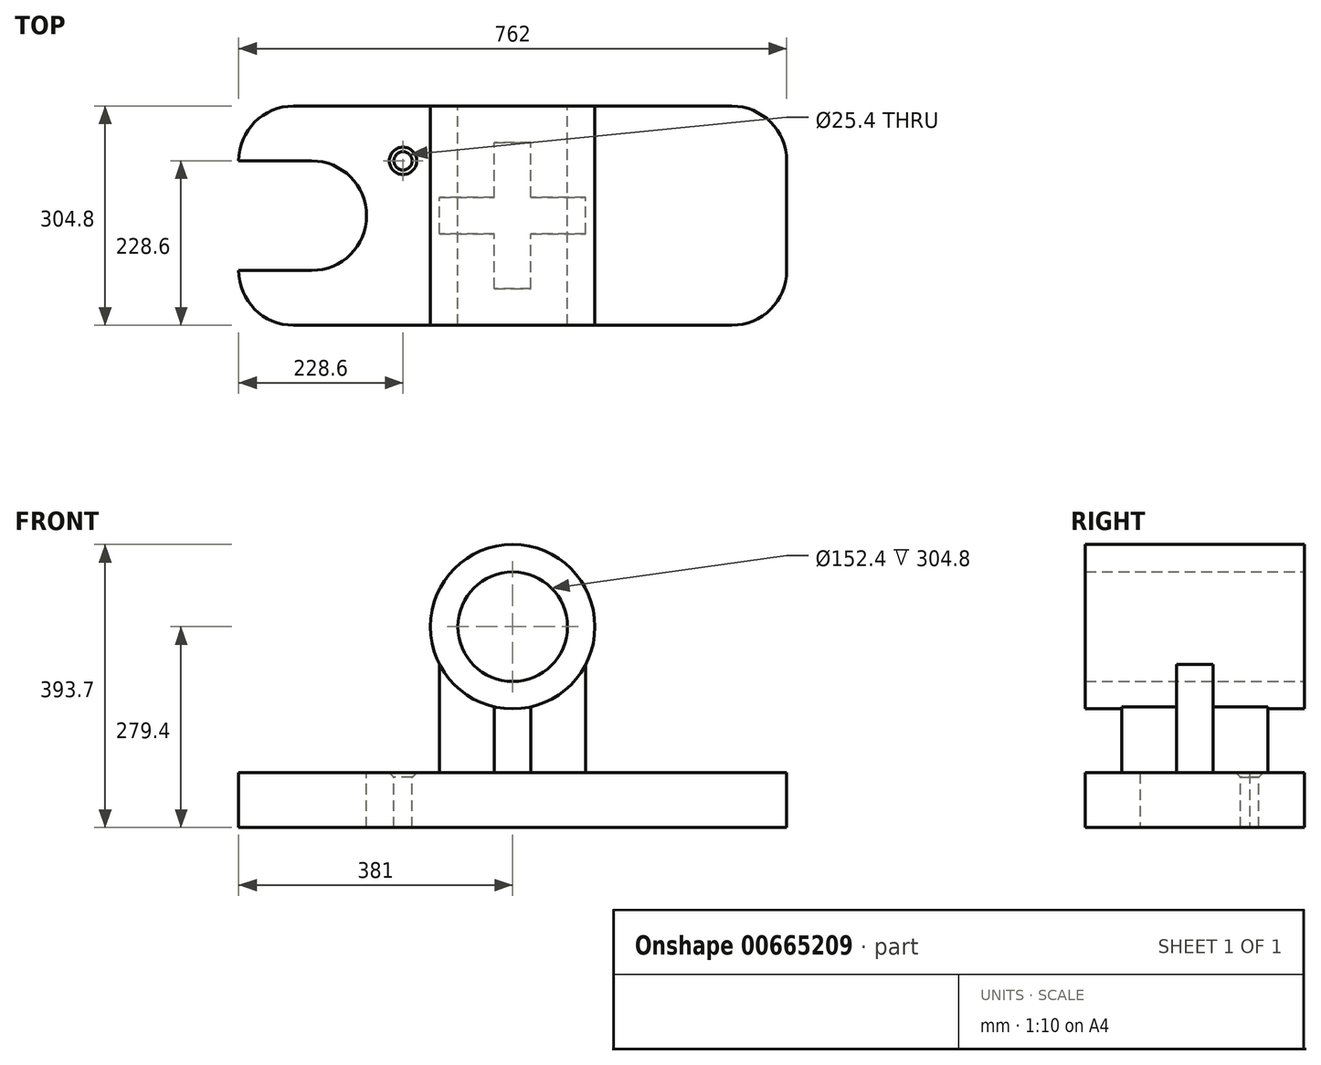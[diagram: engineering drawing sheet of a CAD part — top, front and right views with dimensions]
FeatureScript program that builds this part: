
annotation { "Feature Type Name" : "Feature", "Feature Type Description" : "" }
export const myFeature = defineFeature(function(context is Context, id is Id, definition is map)
    precondition{}
    {
        {
            var Q0;
            Q0=qCreatedBy(makeId("Top.planeOp"),FACE);
            var sketch = newSketch(context, id + "F0", { "sketchPlane" : qUnion([Q0])});
            skLineSegment(sketch, "E0.bottom", {"start": v(381, -152.4) * mm, "end": v(-381, -152.4) * mm});
            skLineSegment(sketch, "E0.top", {"start": v(381, 152.4) * mm, "end": v(-381, 152.4) * mm});
            skLineSegment(sketch, "E0.left", {"start": v(381, -152.4) * mm, "end": v(381, 152.4) * mm});
            skLineSegment(sketch, "E0.right", {"start": v(-381, -152.4) * mm, "end": v(-381, 152.4) * mm});
            skPoint(sketch, "E0.middle", {"position": v(0, 0) * mm});
            skSolve(sketch);
        }
        {
            var Q0;
            Q0=makeQuery(id+"F0.imprint","IMPRINT",FACE,{"disambiguationData":[TD([[makeQuery(id+"F0.imprint","IMPRINT",EDGE,{"derivedFrom":sQuery(id+"F0.wireOp",EDGE,"E0.bottom")}),-1.0]])]});
            extrude(context, id + "F1", {"entities" : qUnion([Q0]), "depth" : 76.2 * mm, "offsetDistance" : 25.4 * mm});
        }
        {
            var Q0;
            Q0=makeQuery(id+"F1.opExtrude","CAP_FACE",FACE,{"disambiguationData":[OSD([sQuery(id+"F0.wireOp",EDGE,"E0.bottom"),sQuery(id+"F0.wireOp",EDGE,"E0.top"),sQuery(id+"F0.wireOp",EDGE,"E0.left"),sQuery(id+"F0.wireOp",EDGE,"E0.right")])],"isStart":false});
            var sketch = newSketch(context, id + "F2", { "sketchPlane" : qUnion([Q0])});
            skLineSegment(sketch, "E1.0", {"start": v(101.6, 25.4) * mm, "end": v(25.4, 25.4) * mm});
            skLineSegment(sketch, "E2.0", {"start": v(101.6, -25.4) * mm, "end": v(25.4, -25.4) * mm});
            skLineSegment(sketch, "E3.0", {"start": v(101.6, -25.4) * mm, "end": v(101.6, 25.4) * mm});
            skLineSegment(sketch, "E4.0", {"start": v(-101.6, -25.4) * mm, "end": v(-101.6, 25.4) * mm});
            skLineSegment(sketch, "E5.0", {"start": v(-25.4, -101.6) * mm, "end": v(-25.4, -25.4) * mm});
            skLineSegment(sketch, "E6.0", {"start": v(25.4, -101.6) * mm, "end": v(25.4, -25.4) * mm});
            skLineSegment(sketch, "E7.trimOffspring", {"start": v(25.4, 101.6) * mm, "end": v(-25.4, 101.6) * mm});
            skLineSegment(sketch, "E8.trimOffspring", {"start": v(25.4, -101.6) * mm, "end": v(-25.4, -101.6) * mm});
            skLineSegment(sketch, "E9.trimOffspring", {"start": v(-25.4, 25.4) * mm, "end": v(-101.6, 25.4) * mm});
            skLineSegment(sketch, "E10.trimOffspring", {"start": v(-25.4, -25.4) * mm, "end": v(-101.6, -25.4) * mm});
            skLineSegment(sketch, "E11.trimOffspring", {"start": v(-25.4, 25.4) * mm, "end": v(-25.4, 101.6) * mm});
            skLineSegment(sketch, "E12.trimOffspring", {"start": v(25.4, 25.4) * mm, "end": v(25.4, 101.6) * mm});
            skSolve(sketch);
        }
        {
            var Q0;
            Q0=makeQuery(id+"F2.imprint","IMPRINT",FACE,{"disambiguationData":[TD([[makeQuery(id+"F2.imprint","IMPRINT",EDGE,{"derivedFrom":sQuery(id+"F2.wireOp",EDGE,"E1.0")}),1.0]])]});
            extrude(context, id + "F3", {"entities" : qUnion([Q0]), "operationType" : NewBodyOperationType.ADD, "depth" : 203.2 * mm, "offsetDistance" : 25.4 * mm});
        }
        {
            var Q0;
            Q0=qCreatedBy(makeId("Front.planeOp"),FACE);
            var sketch = newSketch(context, id + "F4", { "sketchPlane" : qUnion([Q0])});
            skPoint(sketch, "E13.0", {"position": v(0, 279.4) * mm});
            skCircle(sketch, "E14", {"center": v(0, 279.4) * mm, "radius": 114.3 * mm});
            skCircle(sketch, "E15", {"center": v(0, 279.4) * mm, "radius": 76.2 * mm});
            skSolve(sketch);
        }
        {
            var Q0;
            Q0=makeQuery(id+"F4.imprint","IMPRINT",FACE,{"disambiguationData":[TD([[makeQuery(id+"F4.imprint","IMPRINT",EDGE,{"derivedFrom":sQuery(id+"F4.wireOp",EDGE,"E14")}),1.0]])]});
            extrude(context, id + "F5", {"entities" : qUnion([Q0]), "operationType" : NewBodyOperationType.ADD, "endBound" : BoundingType.SYMMETRIC, "depth" : 304.8 * mm, "offsetDistance" : 25.4 * mm});
        }
        {
            var Q0;
            Q0=makeQuery(id+"F4.imprint","IMPRINT",FACE,{"disambiguationData":[TD([[makeQuery(id+"F4.imprint","IMPRINT",EDGE,{"derivedFrom":sQuery(id+"F4.wireOp",EDGE,"E15")}),1.0]])]});
            extrude(context, id + "F6", {"entities" : qUnion([Q0]), "operationType" : NewBodyOperationType.REMOVE, "endBound" : BoundingType.SYMMETRIC, "oppositeDirection" : true, "depth" : 304.8 * mm, "offsetDistance" : 25.4 * mm});
        }
        {
            var Q0;
            Q0=makeQuery(id+"F1.opExtrude","CAP_FACE",FACE,{"disambiguationData":[OSD([sQuery(id+"F0.wireOp",EDGE,"E0.bottom"),sQuery(id+"F0.wireOp",EDGE,"E0.top"),sQuery(id+"F0.wireOp",EDGE,"E0.left"),sQuery(id+"F0.wireOp",EDGE,"E0.right")])],"isStart":false});
            var sketch = newSketch(context, id + "F7", { "sketchPlane" : qUnion([Q0])});
            skSolve(sketch);
        }
        {
            var Q0;
            Q0=makeQuery(id+"F1.opExtrude","SWEPT_EDGE",EDGE,{"disambiguationData":[OSD([sQuery(id+"F0.wireOp",EDGE,"E0.top"),sQuery(id+"F0.wireOp",EDGE,"E0.left")])]});
            var Q1;
            Q1=makeQuery(id+"F1.opExtrude","SWEPT_EDGE",EDGE,{"disambiguationData":[OSD([sQuery(id+"F0.wireOp",EDGE,"E0.top"),sQuery(id+"F0.wireOp",EDGE,"E0.right")])]});
            var Q2;
            Q2=makeQuery(id+"F1.opExtrude","SWEPT_EDGE",EDGE,{"disambiguationData":[OSD([sQuery(id+"F0.wireOp",EDGE,"E0.bottom"),sQuery(id+"F0.wireOp",EDGE,"E0.left")])]});
            var Q3;
            Q3=makeQuery(id+"F1.opExtrude","SWEPT_EDGE",EDGE,{"disambiguationData":[OSD([sQuery(id+"F0.wireOp",EDGE,"E0.bottom"),sQuery(id+"F0.wireOp",EDGE,"E0.right")])]});
            fillet(context, id + "F8", {"entities" : qUnion([Q0, Q1, Q2, Q3]), "radius" : 76.2 * mm, "tangentPropagation" : true, "allowEdgeOverflow" : false});
        }
        {
            var Q0;
            Q0=makeQuery(id+"F7.imprint","IMPRINT",FACE,{"disambiguationData":[TD([[makeQuery(id+"F7.imprint","IMPRINT",EDGE,{"derivedFrom":makeQuery(id+"F1.opExtrude","CAP_EDGE",EDGE,{"disambiguationData":[OSD([sQuery(id+"F0.wireOp",EDGE,"E0.bottom")])],"isStart":false})}),-1.0]])]});
            var sketch = newSketch(context, id + "F9", { "sketchPlane" : qUnion([Q0])});
            skArc(sketch, "E16", {"start": v(-279.4, -76.2) * mm, "mid": v(-203.2, 0) * mm, "end": v(-279.4, 76.2) * mm});
            skLineSegment(sketch, "E17", {"start": v(-279.4, 76.2) * mm, "end": v(-381, 76.2) * mm});
            skLineSegment(sketch, "E18", {"start": v(-279.4, -76.2) * mm, "end": v(-381, -76.2) * mm});
            skPoint(sketch, "E19", {"position": v(-152.4, 76.2) * mm});
            skPoint(sketch, "E20.0", {"position": v(0, 0) * mm});
            skSolve(sketch);
        }
        {
            var Q0;
            Q0=makeQuery(id+"F9.imprint","IMPRINT",FACE,{"disambiguationData":[TD([[makeQuery(id+"F9.imprint","IMPRINT",EDGE,{"derivedFrom":sQuery(id+"F9.wireOp",EDGE,"E16")}),1.0]])]});
            extrude(context, id + "F10", {"entities" : qUnion([Q0]), "operationType" : NewBodyOperationType.REMOVE, "endBound" : BoundingType.THROUGH_ALL, "oppositeDirection" : true, "depth" : 25.4 * mm, "offsetDistance" : 25.4 * mm});
        }
        {
            var Q0;
            Q0=sQuery(id+"F9.wireOp",VERTEX,"E19");
            var Q1;
            Q1=makeQuery(id+"F1.opExtrude","SWEPT_BODY",BODY,{"disambiguationData":[OSD([sQuery(id+"F0.wireOp",EDGE,"E0.bottom"),sQuery(id+"F0.wireOp",EDGE,"E0.top"),sQuery(id+"F0.wireOp",EDGE,"E0.left"),sQuery(id+"F0.wireOp",EDGE,"E0.right")])]});
            hole(context, id + "F11", {"style" : HoleStyle.C_SINK, "endStyle" : HoleEndStyle.THROUGH, "holeDiameter" : 25.4 * mm, "cSinkDiameter" : 38.1 * mm, "cSinkAngle" : 90 * degree, "majorDiameter" : 6.35 * mm, "isTappedThrough" : true, "tappedDepth" : 12.7 * mm, "tapClearance" : 3, "locations" : qUnion([Q0]), "scope" : qUnion([Q1])});
        }
    });
